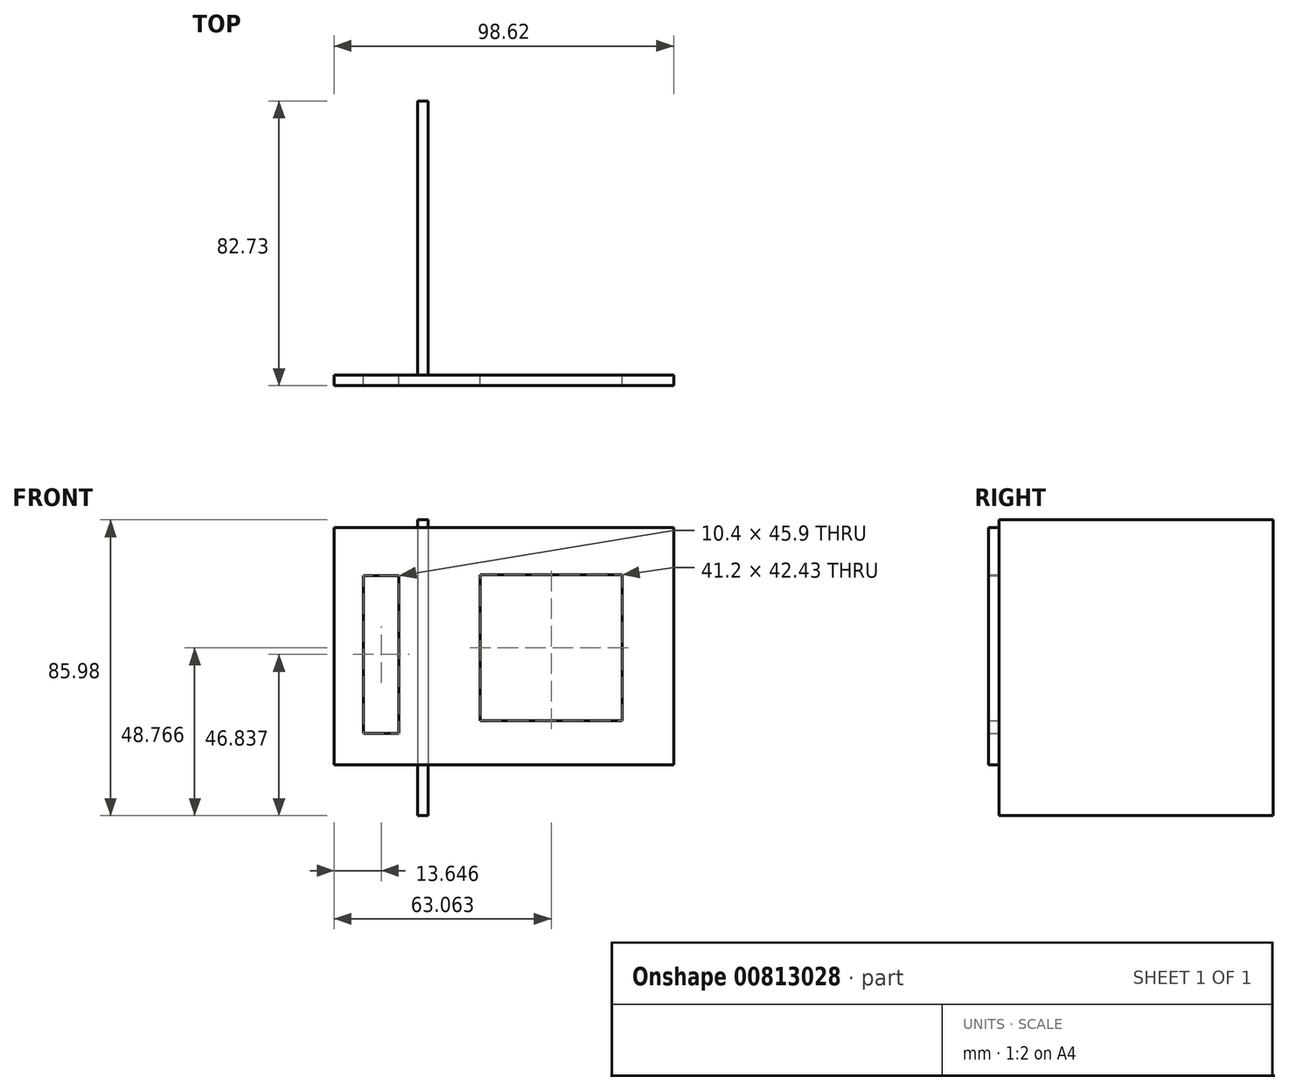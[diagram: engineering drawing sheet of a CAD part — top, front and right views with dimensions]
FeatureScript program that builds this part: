
annotation { "Feature Type Name" : "Feature", "Feature Type Description" : "" }
export const myFeature = defineFeature(function(context is Context, id is Id, definition is map)
    precondition{}
    {
        {
            var Q0;
            Q0=qCreatedBy(makeId("Right.planeOp"),FACE);
            var sketch = newSketch(context, id + "F0", { "sketchPlane" : qUnion([Q0])});
            skLineSegment(sketch, "E0.bottom", {"start": v(-32.22, 36.28) * mm, "end": v(47.51, 36.28) * mm});
            skLineSegment(sketch, "E0.top", {"start": v(-32.22, -49.7) * mm, "end": v(47.51, -49.7) * mm});
            skLineSegment(sketch, "E0.left", {"start": v(-32.22, 36.28) * mm, "end": v(-32.22, -49.7) * mm});
            skLineSegment(sketch, "E0.right", {"start": v(47.51, 36.28) * mm, "end": v(47.51, -49.7) * mm});
            skSolve(sketch);
        }
        {
            var Q0;
            Q0=qSketchRegion(id+"F0",true);
            extrude(context, id + "F1", {"entities" : qUnion([Q0]), "depth" : 3 * mm, "offsetDistance" : 25 * mm, "symmetric" : true});
        }
        {
            var Q0;
            Q0=makeQuery(id+"F1.opExtrude","SWEPT_FACE",FACE,{"disambiguationData":[OSD([sQuery(id+"F0.wireOp",EDGE,"E0.left")])]});
            var sketch = newSketch(context, id + "F2", { "sketchPlane" : qUnion([Q0])});
            skLineSegment(sketch, "E1.bottom", {"start": v(-25.76, 33.96) * mm, "end": v(72.86, 33.96) * mm});
            skLineSegment(sketch, "E1.top", {"start": v(-25.76, -34.9) * mm, "end": v(72.86, -34.9) * mm});
            skLineSegment(sketch, "E1.left", {"start": v(-25.76, 33.96) * mm, "end": v(-25.76, -34.9) * mm});
            skLineSegment(sketch, "E1.right", {"start": v(72.86, 33.96) * mm, "end": v(72.86, -34.9) * mm});
            skPoint(sketch, "E2", {"position": v(0, 15.36) * mm});
            skPoint(sketch, "E3", {"position": v(0, -20.15) * mm});
            skLineSegment(sketch, "E4.bottom", {"start": v(16.7, 20.28) * mm, "end": v(57.9, 20.28) * mm});
            skLineSegment(sketch, "E4.top", {"start": v(16.7, -22.15) * mm, "end": v(57.9, -22.15) * mm});
            skLineSegment(sketch, "E4.left", {"start": v(16.7, 20.28) * mm, "end": v(16.7, -22.15) * mm});
            skLineSegment(sketch, "E4.right", {"start": v(57.9, 20.28) * mm, "end": v(57.9, -22.15) * mm});
            skLineSegment(sketch, "E5.bottom", {"start": v(-17.31, 20.09) * mm, "end": v(-6.92, 20.09) * mm});
            skLineSegment(sketch, "E5.top", {"start": v(-17.31, -25.81) * mm, "end": v(-6.92, -25.81) * mm});
            skLineSegment(sketch, "E5.left", {"start": v(-17.31, 20.09) * mm, "end": v(-17.31, -25.81) * mm});
            skLineSegment(sketch, "E5.right", {"start": v(-6.92, 20.09) * mm, "end": v(-6.92, -25.81) * mm});
            skSolve(sketch);
        }
        {
            var Q0;
            Q0=qSketchRegion(id+"F2",true);
            extrude(context, id + "F3", {"entities" : qUnion([Q0]), "depth" : 3 * mm, "offsetDistance" : 25 * mm});
        }
    });
